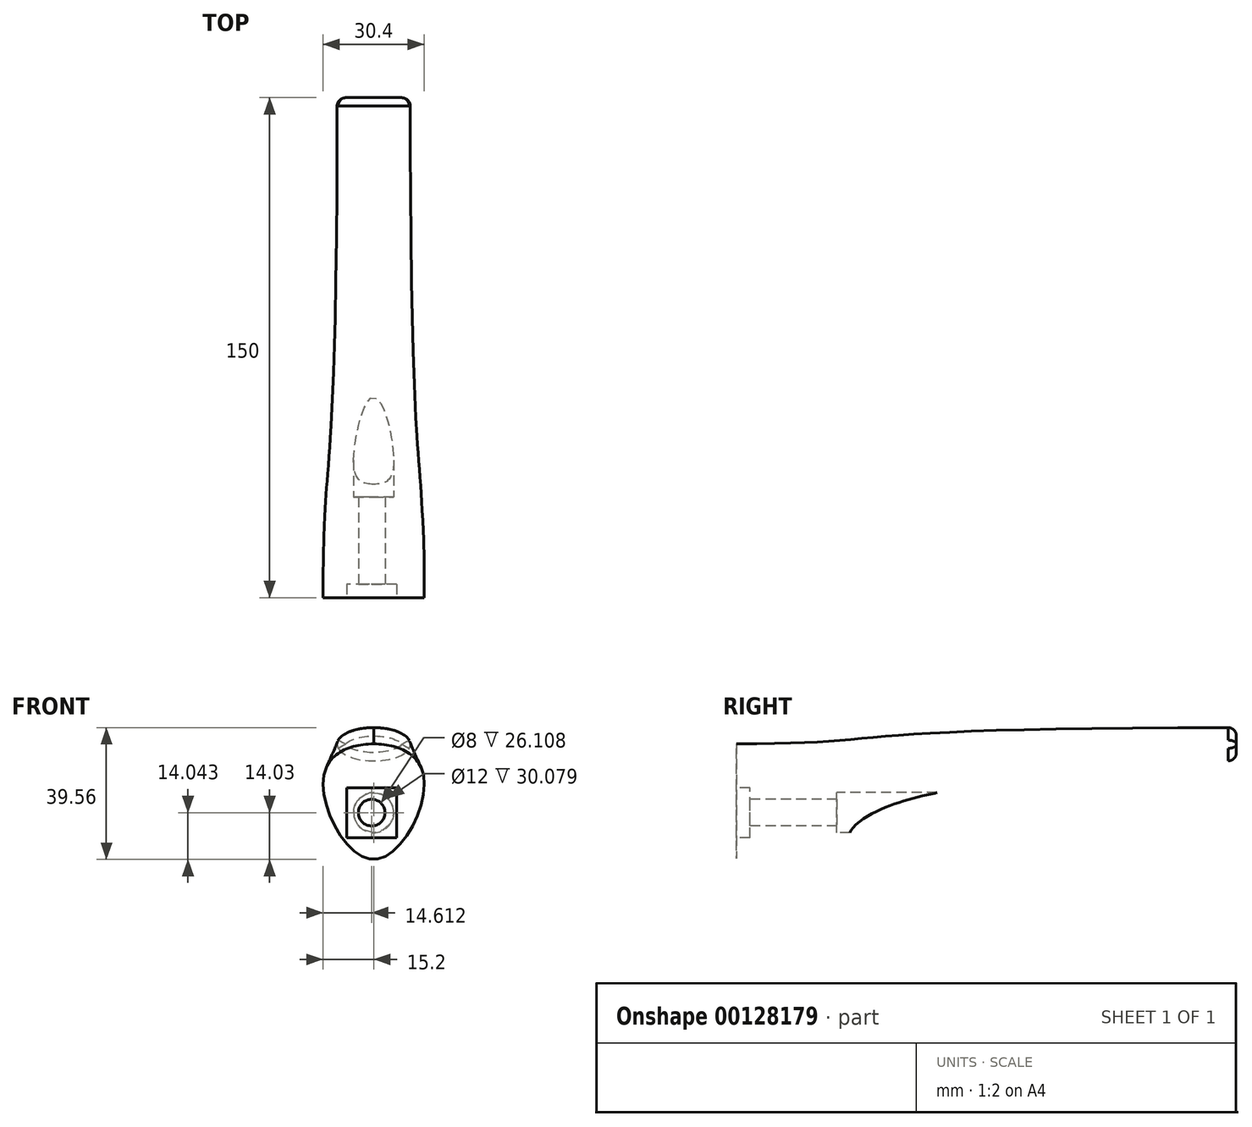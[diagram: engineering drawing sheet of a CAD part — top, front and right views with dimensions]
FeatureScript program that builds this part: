
annotation { "Feature Type Name" : "Feature", "Feature Type Description" : "" }
export const myFeature = defineFeature(function(context is Context, id is Id, definition is map)
    precondition{}
    {
        {
            var Q0;
            Q0=qCreatedBy(makeId("Front.planeOp"),FACE);
            cPlane(context, id + "F0", {"entities" : qUnion([Q0]), "cplaneType" : CPlaneType.OFFSET, "offset" : 75 * mm, "width" : 150 * mm, "height" : 150 * mm});
        }
        {
            var Q0;
            Q0=qCreatedBy(id+"F0.planeOp",FACE);
            var sketch = newSketch(context, id + "F1", { "sketchPlane" : qUnion([Q0])});
            skFitSpline(sketch, "E0", {"points": [v(0, 9.94) * mm, v(15.06, 0) * mm, v(0, -24.73) * mm, v(-15.06, 0) * mm, v(0, 9.94) * mm]});
            skPoint(sketch, "E1", {"position": v(0, -5) * mm});
            skSolve(sketch);
        }
        {
            var Q0;
            Q0=qCreatedBy(makeId("Front.planeOp"),FACE);
            cPlane(context, id + "F2", {"entities" : qUnion([Q0]), "cplaneType" : CPlaneType.OFFSET, "offset" : 75 * mm, "oppositeDirection" : true, "width" : 150 * mm, "height" : 150 * mm});
        }
        {
            var Q0;
            Q0=qCreatedBy(id+"F2.planeOp",FACE);
            var sketch = newSketch(context, id + "F3", { "sketchPlane" : qUnion([Q0])});
            skEllipse(sketch, "E2", {"center": v(0.02, 9.83) * mm, "majorRadius": 10.99 * mm, "minorRadius": 5 * mm, "majorAxis": v(-1, 0)});
            skSolve(sketch);
        }
        {
            var Q0;
            Q0=makeQuery(id+"F1.imprint","IMPRINT",FACE,{"disambiguationData":[TD([[makeQuery(id+"F1.imprint","IMPRINT",EDGE,{"derivedFrom":sQuery(id+"F1.wireOp",EDGE,"E0")}),-1.0]])]});
            var Q1;
            Q1=makeQuery(id+"F3.imprint","IMPRINT",FACE,{"disambiguationData":[TD([[makeQuery(id+"F3.imprint","IMPRINT",EDGE,{"derivedFrom":sQuery(id+"F3.wireOp",EDGE,"E2")}),1.0]])]});
            loft(context, id + "F4", {"startCondition" : LoftEndDerivativeType.NORMAL_TO_PROFILE, "startMagnitude" : 1, "endCondition" : LoftEndDerivativeType.NORMAL_TO_PROFILE, "endMagnitude" : 2.5, "sheetProfilesArray" : [{ "sheetProfileEntities" : qUnion([Q0]) }, { "sheetProfileEntities" : qUnion([Q1]) }]});
        }
        {
            var Q0;
            Q0=qCreatedBy(id+"F0.planeOp",FACE);
            var sketch = newSketch(context, id + "F5", { "sketchPlane" : qUnion([Q0])});
            skPoint(sketch, "E3", {"position": v(-0.59, -35.69) * mm});
            skCircle(sketch, "E4", {"center": v(-0.59, -35.69) * mm, "radius": 4 * mm});
            skSolve(sketch);
        }
        {
            var Q0;
            Q0=makeQuery(id+"F5.imprint","IMPRINT",FACE,{"disambiguationData":[TD([[makeQuery(id+"F5.imprint","IMPRINT",EDGE,{"derivedFrom":sQuery(id+"F5.wireOp",EDGE,"E4")}),1.0]])]});
            var Q1;
            Q1 = qSketchRegion(id + "F5", true);
            extrude(context, id + "F6", {"entities" : qUnion([Q0, Q1]), "oppositeDirection" : true, "depth" : 100 * mm});
        }
        {
            var Q0;
            Q0=makeQuery(id+"F6.opExtrude","CAP_FACE",FACE,{"disambiguationData":[OSD([sQuery(id+"F5.wireOp",EDGE,"E4")])],"isStart":true});
            var sketch = newSketch(context, id + "F7", { "sketchPlane" : qUnion([Q0])});
            skLineSegment(sketch, "E5.bottom", {"start": v(6.91, -43.19) * mm, "end": v(-8.09, -43.19) * mm});
            skLineSegment(sketch, "E5.top", {"start": v(6.91, -28.19) * mm, "end": v(-8.09, -28.19) * mm});
            skLineSegment(sketch, "E5.left", {"start": v(6.91, -43.19) * mm, "end": v(6.91, -28.19) * mm});
            skLineSegment(sketch, "E5.right", {"start": v(-8.09, -43.19) * mm, "end": v(-8.09, -28.19) * mm});
            skPoint(sketch, "E5.middle", {"position": v(-0.59, -35.69) * mm});
            skSolve(sketch);
        }
        {
            var Q0;
            Q0=makeQuery(id+"F7.imprint","IMPRINT",FACE,{"disambiguationData":[TD([[makeQuery(id+"F7.imprint","IMPRINT",EDGE,{"derivedFrom":sQuery(id+"F7.wireOp",EDGE,"E5.bottom")}),-1.0]])]});
            extrude(context, id + "F8", {"entities" : qUnion([Q0]), "operationType" : NewBodyOperationType.ADD, "oppositeDirection" : true, "depth" : 4 * mm});
        }
        {
            var Q0;
            Q0=makeQuery(id+"F6.opExtrude","SWEPT_BODY",BODY,{"disambiguationData":[OSD([sQuery(id+"F5.wireOp",EDGE,"E4")])]});
            transform(context, id + "F9", {"entities" : qUnion([Q0]), "transformType" : TransformType.TRANSLATION_3D, "dx" : 0 * mm, "dy" : 0 * mm, "dz" : 25 * mm, "makeCopy" : false});
        }
        {
            var Q0;
            Q0=makeQuery(id+"F6.opExtrude","SWEPT_BODY",BODY,{"disambiguationData":[OSD([sQuery(id+"F5.wireOp",EDGE,"E4")])]});
            var Q1;
            Q1=makeQuery(id+"F4.opLoft","SWEPT_BODY",BODY,{"disambiguationData":[OSD([makeQuery(id+"F1.imprint","IMPRINT",FACE,{"disambiguationData":[TD([[makeQuery(id+"F1.imprint","IMPRINT",EDGE,{"derivedFrom":sQuery(id+"F1.wireOp",EDGE,"E0")}),-1.0]])]}),makeQuery(id+"F3.imprint","IMPRINT",FACE,{"disambiguationData":[TD([[makeQuery(id+"F3.imprint","IMPRINT",EDGE,{"derivedFrom":sQuery(id+"F3.wireOp",EDGE,"E2")}),1.0]])]})])]});
            booleanBodies(context, id + "F10", {"operationType" : BooleanOperationType.SUBTRACTION, "tools" : qUnion([Q0]), "targets" : qUnion([Q1])});
        }
        {
            var Q0;
            Q0=makeQuery(id+"F4.opLoft","MID_CAP_EDGE",EDGE,{"disambiguationData":[OSD([sQuery(id+"F1.wireOp",EDGE,"E0"),sQuery(id+"F3.wireOp",EDGE,"E2")])],"capPos":1.0});
            fillet(context, id + "F11", {"entities" : qUnion([Q0]), "radius" : 2.5 * mm, "tangentPropagation" : true, "allowEdgeOverflow" : false});
        }
        {
            var Q0;
            Q0=qCreatedBy(makeId("Right.planeOp"),FACE);
            var sketch = newSketch(context, id + "F12", { "sketchPlane" : qUnion([Q0])});
            skLineSegment(sketch, "E6.right", {"start": v(-45.38, -4.7) * mm, "end": v(-45.38, -16.7) * mm});
            skLineSegment(sketch, "E7", {"start": v(-75.04, -10.7) * mm, "end": v(-45.38, -10.7) * mm});
            skPoint(sketch, "E8", {"position": v(-45.38, -10.7) * mm});
            skPoint(sketch, "E9.orphan", {"position": v(-75.04, -16.7) * mm});
            skPoint(sketch, "E6.left.start.orphan", {"position": v(-75.04, -4.7) * mm});
            skLineSegment(sketch, "E10.right", {"start": v(-3.9, -4.7) * mm, "end": v(-3.9, -10.7) * mm});
            skLineSegment(sketch, "E11.bottom", {"start": v(-3.9, -4.7) * mm, "end": v(48.09, -4.7) * mm});
            skLineSegment(sketch, "E11.right", {"start": v(48.09, -4.7) * mm, "end": v(48.09, -10.7) * mm});
            skPoint(sketch, "E12.orphan", {"position": v(-3.9, -16.7) * mm});
            skLineSegment(sketch, "E13.trimOffspring", {"start": v(-3.9, -10.7) * mm, "end": v(48.09, -10.7) * mm});
            skSolve(sketch);
        }
        {
            var Q0;
            Q0=makeQuery(id+"F12.imprint","IMPRINT",FACE,{"disambiguationData":[TD([[makeQuery(id+"F12.imprint","IMPRINT",EDGE,{"derivedFrom":sQuery(id+"F12.wireOp",EDGE,"E11.bottom")}),-1.0]])]});
            var Q1;
            Q1=sQuery(id+"F12.wireOp",EDGE,"E13.trimOffspring");
            revolve(context, id + "F13", {"entities" : qUnion([Q0]), "axis" : qUnion([Q1]), "revolveType" : RevolveType.FULL});
        }
        {
            var Q0;
            Q0=makeQuery(id+"F13.opRevolve","SWEPT_BODY",BODY,{"disambiguationData":[OSD([sQuery(id+"F12.wireOp",EDGE,"E11.bottom"),sQuery(id+"F12.wireOp",EDGE,"E10.right"),sQuery(id+"F12.wireOp",EDGE,"E11.right"),sQuery(id+"F12.wireOp",EDGE,"E13.trimOffspring")])]});
            transform(context, id + "F14", {"entities" : qUnion([Q0]), "transformType" : TransformType.TRANSLATION_3D, "dx" : 0 * mm, "dy" : -41 * mm, "dz" : 0 * mm, "makeCopy" : false});
        }
        {
            var Q0;
            Q0=makeQuery(id+"F13.opRevolve","SWEPT_BODY",BODY,{"disambiguationData":[OSD([sQuery(id+"F12.wireOp",EDGE,"E11.bottom"),sQuery(id+"F12.wireOp",EDGE,"E10.right"),sQuery(id+"F12.wireOp",EDGE,"E11.right"),sQuery(id+"F12.wireOp",EDGE,"E13.trimOffspring")])]});
            var Q1;
            Q1=makeQuery(id+"F4.opLoft","SWEPT_BODY",BODY,{"disambiguationData":[OSD([makeQuery(id+"F1.imprint","IMPRINT",FACE,{"disambiguationData":[TD([[makeQuery(id+"F1.imprint","IMPRINT",EDGE,{"derivedFrom":sQuery(id+"F1.wireOp",EDGE,"E0")}),-1.0]])]}),makeQuery(id+"F3.imprint","IMPRINT",FACE,{"disambiguationData":[TD([[makeQuery(id+"F3.imprint","IMPRINT",EDGE,{"derivedFrom":sQuery(id+"F3.wireOp",EDGE,"E2")}),1.0]])]})])]});
            booleanBodies(context, id + "F15", {"operationType" : BooleanOperationType.SUBTRACTION, "tools" : qUnion([Q0]), "targets" : qUnion([Q1])});
        }
    });
